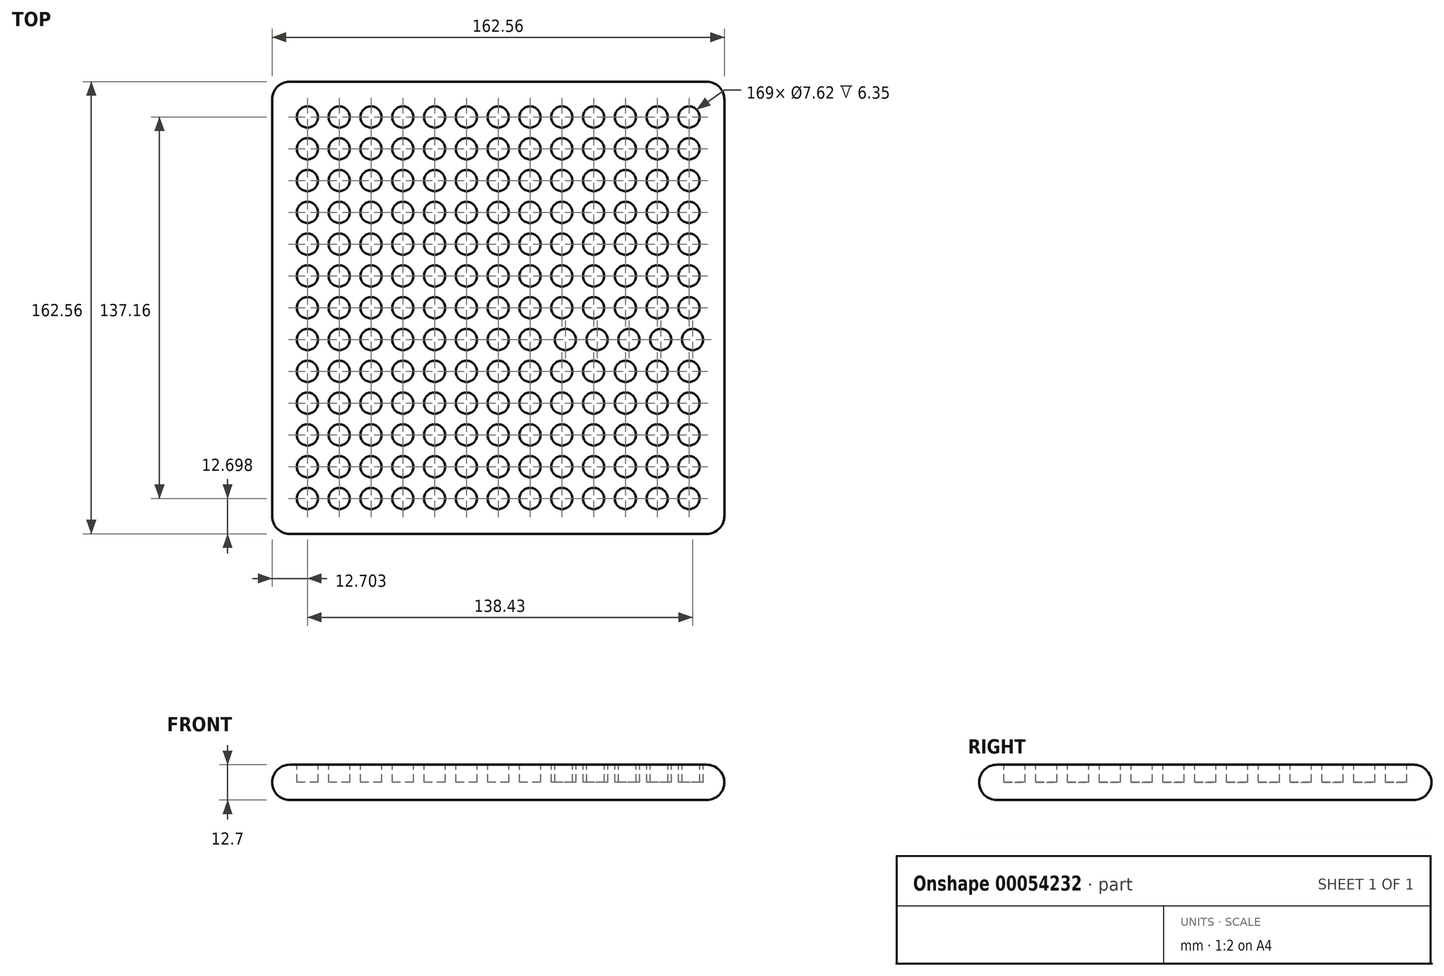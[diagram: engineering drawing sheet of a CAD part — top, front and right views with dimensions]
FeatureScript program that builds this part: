
annotation { "Feature Type Name" : "Feature", "Feature Type Description" : "" }
export const myFeature = defineFeature(function(context is Context, id is Id, definition is map)
    precondition{}
    {
        {
            var Q0;
            Q0=qCreatedBy(makeId("Top.planeOp"),FACE);
            var sketch = newSketch(context, id + "F0", { "sketchPlane" : qUnion([Q0])});
            skLineSegment(sketch, "E0.bottom", {"start": v(-144.62, 173.78) * mm, "end": v(17.94, 173.78) * mm});
            skLineSegment(sketch, "E0.top", {"start": v(-144.62, 11.22) * mm, "end": v(17.94, 11.22) * mm});
            skLineSegment(sketch, "E0.left", {"start": v(-144.62, 173.78) * mm, "end": v(-144.62, 11.22) * mm});
            skLineSegment(sketch, "E0.right", {"start": v(17.94, 173.78) * mm, "end": v(17.94, 11.22) * mm});
            skSolve(sketch);
        }
        {
            var Q0;
            Q0 = qSketchRegion(id + "F0", true);
            extrude(context, id + "F1", {"entities" : qUnion([Q0]), "depth" : 12.7 * mm});
        }
        {
            var Q0;
            Q0=makeQuery(id+"F1.opExtrude","CAP_FACE",FACE,{"disambiguationData":[OSD([sQuery(id+"F0.wireOp",EDGE,"E0.bottom"),sQuery(id+"F0.wireOp",EDGE,"E0.top"),sQuery(id+"F0.wireOp",EDGE,"E0.left"),sQuery(id+"F0.wireOp",EDGE,"E0.right")])],"isStart":false});
            var sketch = newSketch(context, id + "F2", { "sketchPlane" : qUnion([Q0])});
            skSolve(sketch);
        }
        {
            var Q0;
            Q0=makeQuery(id+"F2.imprint","IMPRINT",FACE,{"disambiguationData":[TD([[makeQuery(id+"F2.imprint","IMPRINT",EDGE,{"derivedFrom":makeQuery(id+"F1.opExtrude","CAP_EDGE",EDGE,{"disambiguationData":[OSD([sQuery(id+"F0.wireOp",EDGE,"E0.bottom")])],"isStart":false})}),-1.0]])]});
            var sketch = newSketch(context, id + "F3", { "sketchPlane" : qUnion([Q0])});
            skCircle(sketch, "E1", {"center": v(-131.92, 23.92) * mm, "radius": 3.81 * mm});
            skCircle(sketch, "E2", {"center": v(-86.2, 23.92) * mm, "radius": 3.81 * mm});
            skCircle(sketch, "E3", {"center": v(-40.48, 23.92) * mm, "radius": 3.81 * mm});
            skCircle(sketch, "E4", {"center": v(5.24, 23.92) * mm, "radius": 3.81 * mm});
            skCircle(sketch, "E5", {"center": v(-109.06, 23.92) * mm, "radius": 3.81 * mm});
            skCircle(sketch, "E6", {"center": v(-63.34, 23.92) * mm, "radius": 3.81 * mm});
            skCircle(sketch, "E7", {"center": v(-17.62, 23.92) * mm, "radius": 3.81 * mm});
            skCircle(sketch, "E8", {"center": v(-131.92, 46.78) * mm, "radius": 3.81 * mm});
            skCircle(sketch, "E9", {"center": v(-131.92, 69.64) * mm, "radius": 3.81 * mm});
            skCircle(sketch, "E10", {"center": v(-131.92, 92.5) * mm, "radius": 3.81 * mm});
            skCircle(sketch, "E11", {"center": v(-131.92, 115.36) * mm, "radius": 3.81 * mm});
            skCircle(sketch, "E12", {"center": v(-131.92, 138.22) * mm, "radius": 3.81 * mm});
            skCircle(sketch, "E13", {"center": v(-131.92, 161.08) * mm, "radius": 3.81 * mm});
            skCircle(sketch, "E14", {"center": v(-109.06, 46.78) * mm, "radius": 3.81 * mm});
            skCircle(sketch, "E15", {"center": v(-109.06, 69.64) * mm, "radius": 3.81 * mm});
            skCircle(sketch, "E16", {"center": v(-109.06, 92.5) * mm, "radius": 3.81 * mm});
            skCircle(sketch, "E17", {"center": v(-109.06, 115.36) * mm, "radius": 3.81 * mm});
            skCircle(sketch, "E18", {"center": v(-109.06, 138.22) * mm, "radius": 3.81 * mm});
            skCircle(sketch, "E19", {"center": v(-109.06, 161.08) * mm, "radius": 3.81 * mm});
            skCircle(sketch, "E20", {"center": v(-86.2, 46.78) * mm, "radius": 3.81 * mm});
            skCircle(sketch, "E21", {"center": v(-63.34, 46.78) * mm, "radius": 3.81 * mm});
            skCircle(sketch, "E22", {"center": v(-40.48, 46.78) * mm, "radius": 3.81 * mm});
            skCircle(sketch, "E23", {"center": v(188.12, 46.78) * mm, "radius": 3.81 * mm});
            skCircle(sketch, "E24", {"center": v(5.24, 46.78) * mm, "radius": 3.81 * mm});
            skCircle(sketch, "E25", {"center": v(-17.62, 46.78) * mm, "radius": 3.81 * mm});
            skCircle(sketch, "E26", {"center": v(-86.2, 161.08) * mm, "radius": 3.81 * mm});
            skCircle(sketch, "E27", {"center": v(-86.2, 138.22) * mm, "radius": 3.81 * mm});
            skCircle(sketch, "E28", {"center": v(-86.2, 115.36) * mm, "radius": 3.81 * mm});
            skCircle(sketch, "E29", {"center": v(-86.2, 92.5) * mm, "radius": 3.81 * mm});
            skCircle(sketch, "E30", {"center": v(-86.2, 69.64) * mm, "radius": 3.81 * mm});
            skCircle(sketch, "E31", {"center": v(-63.34, 69.64) * mm, "radius": 3.81 * mm});
            skCircle(sketch, "E32", {"center": v(-40.48, 69.64) * mm, "radius": 3.81 * mm});
            skCircle(sketch, "E33", {"center": v(-17.62, 69.64) * mm, "radius": 3.81 * mm});
            skCircle(sketch, "E34", {"center": v(5.24, 69.64) * mm, "radius": 3.81 * mm});
            skCircle(sketch, "E35", {"center": v(-63.34, 92.5) * mm, "radius": 3.81 * mm});
            skCircle(sketch, "E36", {"center": v(-40.48, 92.5) * mm, "radius": 3.81 * mm});
            skCircle(sketch, "E37", {"center": v(-17.62, 92.5) * mm, "radius": 3.81 * mm});
            skCircle(sketch, "E38", {"center": v(5.24, 92.5) * mm, "radius": 3.81 * mm});
            skCircle(sketch, "E39", {"center": v(-17.62, 161.08) * mm, "radius": 3.81 * mm});
            skCircle(sketch, "E40", {"center": v(-63.34, 115.36) * mm, "radius": 3.81 * mm});
            skCircle(sketch, "E41", {"center": v(-63.34, 161.08) * mm, "radius": 3.81 * mm});
            skCircle(sketch, "E42", {"center": v(-17.62, 138.22) * mm, "radius": 3.81 * mm});
            skCircle(sketch, "E43", {"center": v(-40.48, 138.22) * mm, "radius": 3.81 * mm});
            skCircle(sketch, "E44", {"center": v(-40.48, 161.08) * mm, "radius": 3.81 * mm});
            skCircle(sketch, "E45", {"center": v(5.24, 115.36) * mm, "radius": 3.81 * mm});
            skCircle(sketch, "E46", {"center": v(5.24, 138.22) * mm, "radius": 3.81 * mm});
            skCircle(sketch, "E47", {"center": v(-40.48, 115.36) * mm, "radius": 3.81 * mm});
            skCircle(sketch, "E48", {"center": v(-63.34, 138.22) * mm, "radius": 3.81 * mm});
            skCircle(sketch, "E49", {"center": v(5.24, 161.08) * mm, "radius": 3.81 * mm});
            skCircle(sketch, "E50", {"center": v(-17.62, 115.36) * mm, "radius": 3.81 * mm});
            skCircle(sketch, "E51", {"center": v(-120.49, 161.08) * mm, "radius": 3.81 * mm});
            skCircle(sketch, "E52", {"center": v(-131.92, 149.65) * mm, "radius": 3.81 * mm});
            skCircle(sketch, "E53", {"center": v(-120.49, 149.65) * mm, "radius": 3.81 * mm});
            skCircle(sketch, "E54", {"center": v(-109.06, 149.65) * mm, "radius": 3.81 * mm});
            skCircle(sketch, "E55", {"center": v(-120.49, 138.22) * mm, "radius": 3.81 * mm});
            skCircle(sketch, "E56", {"center": v(-97.63, 161.08) * mm, "radius": 3.81 * mm});
            skCircle(sketch, "E57", {"center": v(-97.63, 149.65) * mm, "radius": 3.81 * mm});
            skCircle(sketch, "E58", {"center": v(-97.63, 138.22) * mm, "radius": 3.81 * mm});
            skCircle(sketch, "E59", {"center": v(-86.2, 149.65) * mm, "radius": 3.81 * mm});
            skCircle(sketch, "E60", {"center": v(-74.77, 161.08) * mm, "radius": 3.81 * mm});
            skCircle(sketch, "E61", {"center": v(-74.77, 149.65) * mm, "radius": 3.81 * mm});
            skCircle(sketch, "E62", {"center": v(-74.77, 138.22) * mm, "radius": 3.81 * mm});
            skCircle(sketch, "E63", {"center": v(-63.34, 149.65) * mm, "radius": 3.81 * mm});
            skCircle(sketch, "E64", {"center": v(-51.9, 161.08) * mm, "radius": 3.81 * mm});
            skCircle(sketch, "E65", {"center": v(-51.9, 149.65) * mm, "radius": 3.81 * mm});
            skCircle(sketch, "E66", {"center": v(-51.9, 138.22) * mm, "radius": 3.81 * mm});
            skCircle(sketch, "E67", {"center": v(-40.48, 149.65) * mm, "radius": 3.81 * mm});
            skCircle(sketch, "E68", {"center": v(-29.05, 161.08) * mm, "radius": 3.81 * mm});
            skCircle(sketch, "E69", {"center": v(-29.05, 149.65) * mm, "radius": 3.81 * mm});
            skCircle(sketch, "E70", {"center": v(-29.05, 138.22) * mm, "radius": 3.81 * mm});
            skCircle(sketch, "E71", {"center": v(-17.62, 149.65) * mm, "radius": 3.81 * mm});
            skCircle(sketch, "E72", {"center": v(-6.19, 161.08) * mm, "radius": 3.81 * mm});
            skCircle(sketch, "E73", {"center": v(-6.19, 149.65) * mm, "radius": 3.81 * mm});
            skCircle(sketch, "E74", {"center": v(5.24, 149.65) * mm, "radius": 3.81 * mm});
            skCircle(sketch, "E75", {"center": v(-6.19, 138.22) * mm, "radius": 3.81 * mm});
            skCircle(sketch, "E76", {"center": v(-131.92, 126.79) * mm, "radius": 3.81 * mm});
            skCircle(sketch, "E77", {"center": v(-131.92, 103.93) * mm, "radius": 3.81 * mm});
            skCircle(sketch, "E78", {"center": v(-120.49, 126.79) * mm, "radius": 3.81 * mm});
            skCircle(sketch, "E79", {"center": v(-109.06, 126.79) * mm, "radius": 3.81 * mm});
            skCircle(sketch, "E80", {"center": v(-120.49, 115.36) * mm, "radius": 3.81 * mm});
            skCircle(sketch, "E81", {"center": v(-120.49, 103.93) * mm, "radius": 3.81 * mm});
            skCircle(sketch, "E82", {"center": v(-109.06, 103.93) * mm, "radius": 3.81 * mm});
            skCircle(sketch, "E83", {"center": v(-120.49, 92.5) * mm, "radius": 3.81 * mm});
            skCircle(sketch, "E84", {"center": v(-120.49, 81.07) * mm, "radius": 3.81 * mm});
            skCircle(sketch, "E85", {"center": v(-109.06, 81.07) * mm, "radius": 3.81 * mm});
            skCircle(sketch, "E86", {"center": v(-131.92, 81.07) * mm, "radius": 3.81 * mm});
            skCircle(sketch, "E87", {"center": v(-120.49, 69.64) * mm, "radius": 3.81 * mm});
            skCircle(sketch, "E88", {"center": v(-109.06, 58.2) * mm, "radius": 3.81 * mm});
            skCircle(sketch, "E89", {"center": v(-120.49, 58.2) * mm, "radius": 3.81 * mm});
            skCircle(sketch, "E90", {"center": v(-131.92, 58.2) * mm, "radius": 3.81 * mm});
            skCircle(sketch, "E91", {"center": v(-120.49, 46.78) * mm, "radius": 3.81 * mm});
            skCircle(sketch, "E92", {"center": v(-120.49, 23.92) * mm, "radius": 3.81 * mm});
            skCircle(sketch, "E93", {"center": v(-120.49, 35.35) * mm, "radius": 3.81 * mm});
            skCircle(sketch, "E94", {"center": v(-109.06, 35.35) * mm, "radius": 3.81 * mm});
            skCircle(sketch, "E95", {"center": v(-131.92, 35.35) * mm, "radius": 3.81 * mm});
            skCircle(sketch, "E96", {"center": v(-97.63, 126.79) * mm, "radius": 3.81 * mm});
            skCircle(sketch, "E97", {"center": v(-86.2, 126.79) * mm, "radius": 3.81 * mm});
            skCircle(sketch, "E98", {"center": v(-97.63, 115.36) * mm, "radius": 3.81 * mm});
            skCircle(sketch, "E99", {"center": v(-74.77, 115.36) * mm, "radius": 3.81 * mm});
            skCircle(sketch, "E100", {"center": v(-74.77, 126.79) * mm, "radius": 3.81 * mm});
            skCircle(sketch, "E101", {"center": v(-63.34, 126.79) * mm, "radius": 3.81 * mm});
            skCircle(sketch, "E102", {"center": v(-51.9, 126.79) * mm, "radius": 3.81 * mm});
            skCircle(sketch, "E103", {"center": v(-51.9, 115.36) * mm, "radius": 3.81 * mm});
            skCircle(sketch, "E104", {"center": v(-40.48, 126.79) * mm, "radius": 3.81 * mm});
            skCircle(sketch, "E105", {"center": v(-29.05, 126.79) * mm, "radius": 3.81 * mm});
            skCircle(sketch, "E106", {"center": v(-17.62, 126.79) * mm, "radius": 3.81 * mm});
            skCircle(sketch, "E107", {"center": v(-29.05, 115.36) * mm, "radius": 3.81 * mm});
            skCircle(sketch, "E108", {"center": v(-6.19, 126.79) * mm, "radius": 3.81 * mm});
            skCircle(sketch, "E109", {"center": v(5.24, 126.79) * mm, "radius": 3.81 * mm});
            skCircle(sketch, "E110", {"center": v(-6.19, 115.36) * mm, "radius": 3.81 * mm});
            skCircle(sketch, "E111", {"center": v(-97.63, 103.93) * mm, "radius": 3.81 * mm});
            skCircle(sketch, "E112", {"center": v(-97.63, 92.5) * mm, "radius": 3.81 * mm});
            skCircle(sketch, "E113", {"center": v(-86.2, 103.93) * mm, "radius": 3.81 * mm});
            skCircle(sketch, "E114", {"center": v(-74.77, 103.93) * mm, "radius": 3.81 * mm});
            skCircle(sketch, "E115", {"center": v(-74.77, 92.5) * mm, "radius": 3.81 * mm});
            skCircle(sketch, "E116", {"center": v(-63.34, 103.93) * mm, "radius": 3.81 * mm});
            skCircle(sketch, "E117", {"center": v(-51.9, 103.93) * mm, "radius": 3.81 * mm});
            skCircle(sketch, "E118", {"center": v(-51.9, 92.5) * mm, "radius": 3.81 * mm});
            skCircle(sketch, "E119", {"center": v(-40.48, 103.93) * mm, "radius": 3.81 * mm});
            skCircle(sketch, "E120", {"center": v(-29.05, 103.93) * mm, "radius": 3.81 * mm});
            skCircle(sketch, "E121", {"center": v(-29.05, 92.5) * mm, "radius": 3.81 * mm});
            skCircle(sketch, "E122", {"center": v(-17.62, 103.93) * mm, "radius": 3.81 * mm});
            skCircle(sketch, "E123", {"center": v(-6.19, 103.93) * mm, "radius": 3.81 * mm});
            skCircle(sketch, "E124", {"center": v(5.24, 103.93) * mm, "radius": 3.81 * mm});
            skCircle(sketch, "E125", {"center": v(-6.19, 92.5) * mm, "radius": 3.81 * mm});
            skCircle(sketch, "E126", {"center": v(-39.2, 81.07) * mm, "radius": 3.81 * mm});
            skCircle(sketch, "E127", {"center": v(-27.78, 81.07) * mm, "radius": 3.81 * mm});
            skCircle(sketch, "E128", {"center": v(-29.05, 69.64) * mm, "radius": 3.81 * mm});
            skCircle(sketch, "E129", {"center": v(-16.35, 81.07) * mm, "radius": 3.81 * mm});
            skCircle(sketch, "E130", {"center": v(-4.92, 81.07) * mm, "radius": 3.81 * mm});
            skCircle(sketch, "E131", {"center": v(6.51, 81.07) * mm, "radius": 3.81 * mm});
            skCircle(sketch, "E132", {"center": v(-6.19, 69.64) * mm, "radius": 3.81 * mm});
            skCircle(sketch, "E133", {"center": v(5.24, 58.2) * mm, "radius": 3.81 * mm});
            skCircle(sketch, "E134", {"center": v(-6.19, 58.2) * mm, "radius": 3.81 * mm});
            skCircle(sketch, "E135", {"center": v(-29.05, 58.2) * mm, "radius": 3.81 * mm});
            skCircle(sketch, "E136", {"center": v(-17.62, 58.2) * mm, "radius": 3.81 * mm});
            skCircle(sketch, "E137", {"center": v(-29.05, 46.78) * mm, "radius": 3.81 * mm});
            skCircle(sketch, "E138", {"center": v(-6.19, 46.78) * mm, "radius": 3.81 * mm});
            skCircle(sketch, "E139", {"center": v(-29.05, 35.35) * mm, "radius": 3.81 * mm});
            skCircle(sketch, "E140", {"center": v(-40.48, 35.35) * mm, "radius": 3.81 * mm});
            skCircle(sketch, "E141", {"center": v(-17.62, 35.35) * mm, "radius": 3.81 * mm});
            skCircle(sketch, "E142", {"center": v(-6.19, 35.35) * mm, "radius": 3.81 * mm});
            skCircle(sketch, "E143", {"center": v(5.24, 35.35) * mm, "radius": 3.81 * mm});
            skCircle(sketch, "E144", {"center": v(-29.05, 23.92) * mm, "radius": 3.81 * mm});
            skCircle(sketch, "E145", {"center": v(-6.19, 23.92) * mm, "radius": 3.81 * mm});
            skCircle(sketch, "E146", {"center": v(-40.48, 58.2) * mm, "radius": 3.81 * mm});
            skCircle(sketch, "E147", {"center": v(-86.2, 81.07) * mm, "radius": 3.81 * mm});
            skCircle(sketch, "E148", {"center": v(-74.77, 81.07) * mm, "radius": 3.81 * mm});
            skCircle(sketch, "E149", {"center": v(-63.34, 81.07) * mm, "radius": 3.81 * mm});
            skCircle(sketch, "E150", {"center": v(-97.63, 81.07) * mm, "radius": 3.81 * mm});
            skCircle(sketch, "E151", {"center": v(-97.63, 69.64) * mm, "radius": 3.81 * mm});
            skCircle(sketch, "E152", {"center": v(-74.77, 69.64) * mm, "radius": 3.81 * mm});
            skCircle(sketch, "E153", {"center": v(-51.9, 69.64) * mm, "radius": 3.81 * mm});
            skCircle(sketch, "E154", {"center": v(-51.9, 81.07) * mm, "radius": 3.81 * mm});
            skCircle(sketch, "E155", {"center": v(-97.63, 58.2) * mm, "radius": 3.81 * mm});
            skCircle(sketch, "E156", {"center": v(-86.2, 58.2) * mm, "radius": 3.81 * mm});
            skCircle(sketch, "E157", {"center": v(-74.77, 58.2) * mm, "radius": 3.81 * mm});
            skCircle(sketch, "E158", {"center": v(-63.34, 58.2) * mm, "radius": 3.81 * mm});
            skCircle(sketch, "E159", {"center": v(-51.9, 58.2) * mm, "radius": 3.81 * mm});
            skCircle(sketch, "E160", {"center": v(-51.9, 46.78) * mm, "radius": 3.81 * mm});
            skCircle(sketch, "E161", {"center": v(-51.9, 35.35) * mm, "radius": 3.81 * mm});
            skCircle(sketch, "E162", {"center": v(-51.9, 23.92) * mm, "radius": 3.81 * mm});
            skCircle(sketch, "E163", {"center": v(-63.34, 35.35) * mm, "radius": 3.81 * mm});
            skCircle(sketch, "E164", {"center": v(-74.77, 46.78) * mm, "radius": 3.81 * mm});
            skCircle(sketch, "E165", {"center": v(-74.77, 35.35) * mm, "radius": 3.81 * mm});
            skCircle(sketch, "E166", {"center": v(-74.77, 23.92) * mm, "radius": 3.81 * mm});
            skCircle(sketch, "E167", {"center": v(-86.2, 35.35) * mm, "radius": 3.81 * mm});
            skCircle(sketch, "E168", {"center": v(-97.63, 46.78) * mm, "radius": 3.81 * mm});
            skCircle(sketch, "E169", {"center": v(-97.63, 35.35) * mm, "radius": 3.81 * mm});
            skCircle(sketch, "E170", {"center": v(-97.63, 23.92) * mm, "radius": 3.81 * mm});
            skSolve(sketch);
        }
        {
            var Q0;
            Q0 = qSketchRegion(id + "F3", true);
            extrude(context, id + "F4", {"entities" : qUnion([Q0]), "operationType" : NewBodyOperationType.REMOVE, "oppositeDirection" : true, "depth" : 6.35 * mm});
        }
        {
            var Q0;
            Q0=makeQuery(id+"F1.opExtrude","SWEPT_FACE",FACE,{"disambiguationData":[OSD([sQuery(id+"F0.wireOp",EDGE,"E0.top")])]});
            var Q1;
            Q1=makeQuery(id+"F1.opExtrude","SWEPT_FACE",FACE,{"disambiguationData":[OSD([sQuery(id+"F0.wireOp",EDGE,"E0.left")])]});
            var Q2;
            Q2=makeQuery(id+"F1.opExtrude","SWEPT_FACE",FACE,{"disambiguationData":[OSD([sQuery(id+"F0.wireOp",EDGE,"E0.bottom")])]});
            var Q3;
            Q3=makeQuery(id+"F1.opExtrude","SWEPT_FACE",FACE,{"disambiguationData":[OSD([sQuery(id+"F0.wireOp",EDGE,"E0.right")])]});
            fillet(context, id + "F5", {"entities" : qUnion([Q0, Q1, Q2, Q3]), "radius" : 6.35 * mm, "tangentPropagation" : true, "allowEdgeOverflow" : false});
        }
    });
